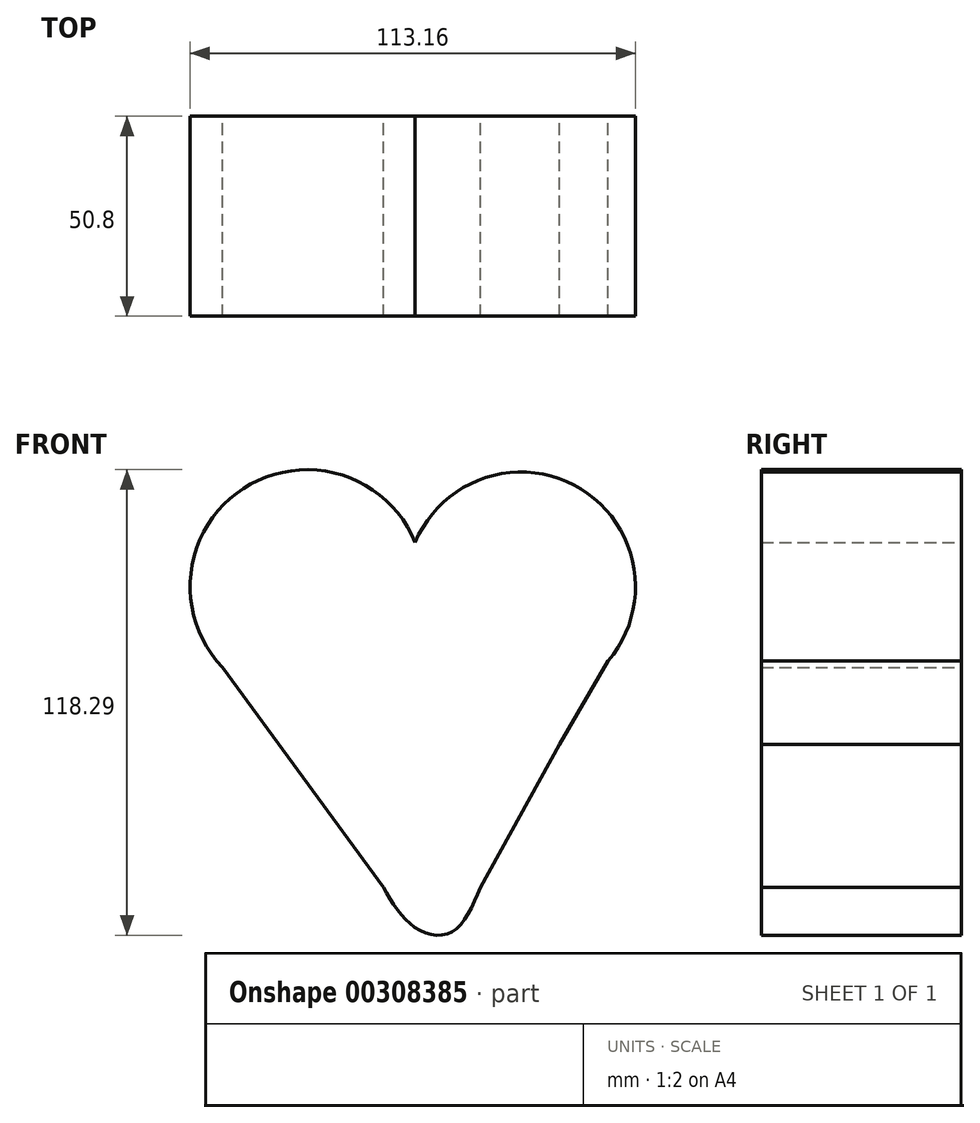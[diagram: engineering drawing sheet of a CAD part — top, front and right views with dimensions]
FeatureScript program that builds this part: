
annotation { "Feature Type Name" : "Feature", "Feature Type Description" : "" }
export const myFeature = defineFeature(function(context is Context, id is Id, definition is map)
    precondition{}
    {
        {
            var Q0;
            Q0=qCreatedBy(makeId("Front.planeOp"),FACE);
            var sketch = newSketch(context, id + "F0", { "sketchPlane" : qUnion([Q0])});
            skCircle(sketch, "E0", {"center": v(-33.52, 30.2) * mm, "radius": 29.7 * mm});
            skCircle(sketch, "E1", {"center": v(20.83, 30.2) * mm, "radius": 29.1 * mm});
            skLineSegment(sketch, "E2", {"start": v(-55.01, 9.7) * mm, "end": v(-14.14, -46.17) * mm});
            skFitSpline(sketch, "E3", {"points": [v(-14.14, -46.17) * mm, v(-6.19, -56.34) * mm, v(3.1, -57.66) * mm, v(10.6, -46.17) * mm], "startDerivative": vector(19.85, -34.01) * mm, "endDerivative": vector(17.44, 41.04) * mm});
            skLineSegment(sketch, "E4", {"start": v(10.6, -46.17) * mm, "end": v(41.48, 9.7) * mm});
            skLineSegment(sketch, "E5", {"start": v(48.21, 20.35) * mm, "end": v(30.66, -9.89) * mm});
            skLineSegment(sketch, "E6", {"start": v(49.59, 25.73) * mm, "end": v(30.66, -9.89) * mm});
            skLineSegment(sketch, "E7", {"start": v(-61.55, 20.35) * mm, "end": v(-36.6, -13.74) * mm});
            skLineSegment(sketch, "E8", {"start": v(-60.08, 16.9) * mm, "end": v(-40.49, -9.89) * mm});
            skSolve(sketch);
        }
        {
            var Q0;
            Q0 = qSketchRegion(id + "F0", true);
            extrude(context, id + "F1", {"entities" : qUnion([Q0]), "depth" : 50.8 * mm});
        }
    });
